# Revit family: ITK by ZPAS__Органайзер кабельный горизонтальный 19
name_source: partatom
category: Обобщенные модели
units: mm (PartAtom-declared; Revit-internal decimal feet)

## family parameters
Всегда вертикально = Да
Может служить основой для арматурных стержней = Нет
На основе рабочей плоскости = Нет
Общий = Нет
При загрузке вырезать с полостями = Нет
Размер круглого соединителя = Использовать диаметр
Тип детали = Нормальный
Точка расчета площади = Нет

## types (2) — shared parameters
ADSK_URL страницы изделия = https://www.itk-group.ru
ADSK_Версия Revit = 2019
ADSK_Версия семейства = 1.0
ADSK_Группирование = I. ЩИТЫ И ПУЛЬТЫ
ADSK_Единица измерения = шт
ADSK_Завод-изготовитель = IEK
ADSK_Марка = by ZPAS
ADSK_Материал наименование = Листовая сталь
IEK_URL = https://www.itk-group.ru
IEK_Описание = Органайзеры крепятся к каркасу шкафа.
KSI_CMa_Строительные материалы = 10.03.02.06
KSI_CPr_Строительные изделия = 61.1.04.08
URL = https://www.iek.ru
Высота = 100 мм
Глубина = 20 мм
Изготовитель = ITK
Материал = Окраска - RAL 7035
Тип монтажа = Установка на захваты

## per-type parameters (varying)
| type | ADSK_Код изделия | ADSK_Масса | ADSK_Наименование | IEK_Цена за единицу | Ширина |
| Ш1000 | ZP-CO-H-1000 | 0.3 | ITK by ZPAS Органайзер кабельный горизонтальный 19" 1000 | 4133.77 | 1000 мм |
| Ш1200 | ZP-CO-H-1200 | 0.4 | ITK by ZPAS Органайзер кабельный горизонтальный 19" 1200 | 4324.48 | 1200 мм |
